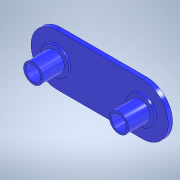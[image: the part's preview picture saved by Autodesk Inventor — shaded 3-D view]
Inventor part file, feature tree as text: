
AUTODESK INVENTOR PART (.ipt)
format: ipt  version: 2022 (Build 260153000, 153)  size: 139,776 bytes
history: native  units: in
note: dims shown in document units (in); Inventor stores cm internally (conversion verified against a paired STEP export)
features: extrude x3, sketch x3, projected_geometry x1
ambient origin geometry x8: Origin, YZ Plane, XZ Plane, XY Plane, X Axis, Y Axis, Z Axis, Center Point
bodies: Solid1 (feature_tree)
feature tree (7):
  extrude  "Extrusion1"  Depth=0.2362in
  extrude  "Extrusion2"  Depth=0.0394in TaperAngle=0.0deg
  extrude  "Extrusion3"  Depth=0.0197in
  sketch  "Sketch1"  dims[d0=0.7874in d1=0.2362in]
  sketch  "Sketch2"  dims[d2=0.1339in d3=0.0394in d4=0.0in]
  sketch  "Sketch3"  dims[d5=0.1772in d6=0.1772in d7=0.2165in d8=0.0in d9=0.2559in d10=0.0197in d11=0.0in]
  projected_geometry  "Projected Loop1"
